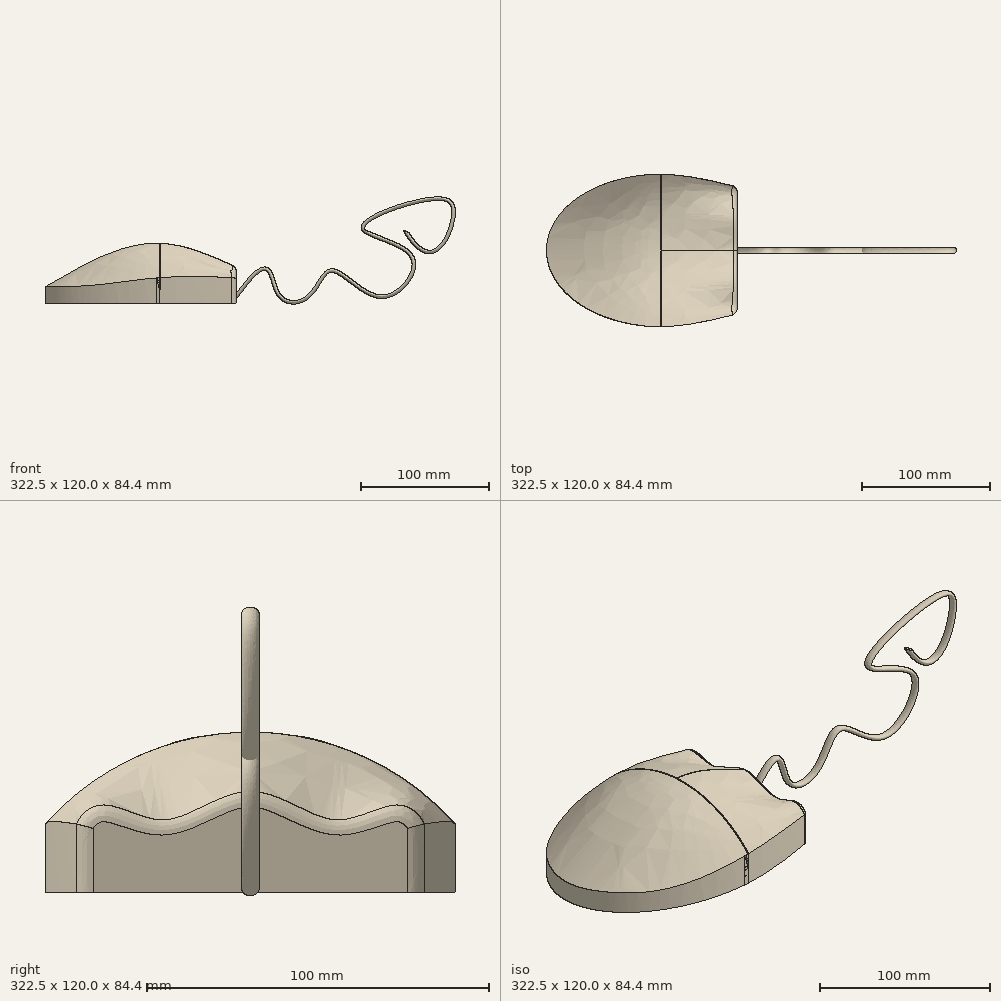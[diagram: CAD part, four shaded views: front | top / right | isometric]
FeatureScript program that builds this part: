
annotation { "Feature Type Name" : "Feature", "Feature Type Description" : "" }
export const myFeature = defineFeature(function(context is Context, id is Id, definition is map)
    precondition{}
    {
        {
            var Q0;
            Q0=qCreatedBy(makeId("Right.planeOp"),FACE);
            cPlane(context, id + "F0", {"entities" : qUnion([Q0]), "cplaneType" : CPlaneType.OFFSET, "offset" : 60 * mm, "width" : 150 * mm, "height" : 150 * mm});
        }
        {
            var Q0;
            Q0=qCreatedBy(makeId("Right.planeOp"),FACE);
            var Q1;
            Q1 = qBodyType(qCreatedBy(id + "F3" ,EDGE), BodyType.WIRE);
            cPlane(context, id + "F1", {"entities" : qUnion([Q0, Q1]), "cplaneType" : CPlaneType.OFFSET, "offset" : 90 * mm, "oppositeDirection" : true, "width" : 150 * mm, "height" : 150 * mm});
        }
        {
            var Q0;
            Q0=qCreatedBy(id+"F1.planeOp",FACE);
            var sketch = newSketch(context, id + "F2", { "sketchPlane" : qUnion([Q0])});
            skLineSegment(sketch, "E0", {"start": v(-40, 0) * mm, "end": v(-40, 2) * mm});
            skLineSegment(sketch, "E1", {"start": v(40, 2) * mm, "end": v(40, 0) * mm});
            skLineSegment(sketch, "E2", {"start": v(-40, 0) * mm, "end": v(40, 0) * mm});
            skArc(sketch, "E3", {"start": v(40, 2) * mm, "mid": v(0, 12.72) * mm, "end": v(-40, 2) * mm});
            skSolve(sketch);
        }
        {
            var Q0;
            Q0=qCreatedBy(id+"F0.planeOp",FACE);
            var sketch = newSketch(context, id + "F3", { "sketchPlane" : qUnion([Q0])});
            skLineSegment(sketch, "E4", {"start": v(-50, 0) * mm, "end": v(50, 0) * mm});
            skLineSegment(sketch, "E5", {"start": v(-50, 0) * mm, "end": v(-50, 20) * mm});
            skLineSegment(sketch, "E6", {"start": v(50, 20) * mm, "end": v(50, 0) * mm});
            skFitSpline(sketch, "E7", {"points": [v(-50, 20) * mm, v(-43, 25) * mm, v(-25, 20) * mm, v(0, 28.4) * mm, v(25, 20) * mm, v(43, 25) * mm, v(50, 20) * mm], "startDerivative": vector(27.74, 64.52) * mm, "endDerivative": vector(29, -66.62) * mm});
            skSolve(sketch);
        }
        {
            var Q0;
            Q0=qCreatedBy(makeId("Right.planeOp"),FACE);
            var sketch = newSketch(context, id + "F4", { "sketchPlane" : qUnion([Q0])});
            skLineSegment(sketch, "E8", {"start": v(-60, 0) * mm, "end": v(60, 0) * mm});
            skLineSegment(sketch, "E9", {"start": v(-60, 0) * mm, "end": v(-60, 20) * mm});
            skLineSegment(sketch, "E10", {"start": v(60, 20) * mm, "end": v(60, 0) * mm});
            skArc(sketch, "E11", {"start": v(60, 20) * mm, "mid": v(0, 47.08) * mm, "end": v(-60, 20) * mm});
            skSolve(sketch);
        }
        {
            var Q0;
            Q0=makeQuery(id+"F2.imprint","IMPRINT",FACE,{"disambiguationData":[TD([[makeQuery(id+"F2.imprint","IMPRINT",EDGE,{"derivedFrom":sQuery(id+"F2.wireOp",EDGE,"E0")}),-1.0]])]});
            var Q1;
            Q1=makeQuery(id+"F4.imprint","IMPRINT",FACE,{"disambiguationData":[TD([[makeQuery(id+"F4.imprint","IMPRINT",EDGE,{"derivedFrom":sQuery(id+"F4.wireOp",EDGE,"E8")}),1.0]])]});
            var Q2;
            Q2=makeQuery(id+"F3.imprint","IMPRINT",FACE,{"disambiguationData":[TD([[makeQuery(id+"F3.imprint","IMPRINT",EDGE,{"derivedFrom":sQuery(id+"F3.wireOp",EDGE,"E4")}),1.0]])]});
            loft(context, id + "F5", {"sheetProfilesArray" : [{ "sheetProfileEntities" : qUnion([Q0]) }, { "sheetProfileEntities" : qUnion([Q1]) }, { "sheetProfileEntities" : qUnion([Q2]) }]});
        }
        {
            var Q0;
            Q0=qCreatedBy(makeId("Top.planeOp"),FACE);
            cPlane(context, id + "F6", {"entities" : qUnion([Q0]), "cplaneType" : CPlaneType.OFFSET, "offset" : 47.08 * mm, "width" : 150 * mm, "height" : 150 * mm});
        }
        {
            var Q0;
            Q0=qCreatedBy(id+"F6.planeOp",FACE);
            var sketch = newSketch(context, id + "F7", { "sketchPlane" : qUnion([Q0])});
            skLineSegment(sketch, "E12.bottom", {"start": v(0, 60) * mm, "end": v(0.5, 60) * mm});
            skLineSegment(sketch, "E12.top", {"start": v(0, -60) * mm, "end": v(0.5, -60) * mm});
            skLineSegment(sketch, "E12.left", {"start": v(0, 60) * mm, "end": v(0, -60) * mm});
            skLineSegment(sketch, "E12.right", {"start": v(0.5, 60) * mm, "end": v(0.5, -60) * mm});
            skLineSegment(sketch, "E13.bottom", {"start": v(0, 0.25) * mm, "end": v(60, 0.25) * mm});
            skLineSegment(sketch, "E13.top", {"start": v(0, -0.25) * mm, "end": v(60, -0.25) * mm});
            skLineSegment(sketch, "E13.left", {"start": v(0, 0.25) * mm, "end": v(0, -0.25) * mm});
            skLineSegment(sketch, "E13.right", {"start": v(60, 0.25) * mm, "end": v(60, -0.25) * mm});
            skSolve(sketch);
        }
        {
            var Q0;
            Q0 = qSketchRegion(id + "F7", true);
            extrude(context, id + "F8", {"entities" : qUnion([Q0]), "operationType" : NewBodyOperationType.REMOVE, "oppositeDirection" : true, "depth" : 37 * mm, "offsetDistance" : 25 * mm});
        }
        {
            var Q0;
            Q0=qCreatedBy(makeId("Top.planeOp"),FACE);
            var sketch = newSketch(context, id + "F9", { "sketchPlane" : qUnion([Q0])});
            skEllipticalArc(sketch, "E14", {});
            skPoint(sketch, "E15", {"position": v(0, -60) * mm});
            skPoint(sketch, "E16", {"position": v(0, 60) * mm});
            skPoint(sketch, "E17", {"position": v(-89.99, -40.02) * mm});
            skPoint(sketch, "E18", {"position": v(-89.99, 39.96) * mm});
            skLineSegment(sketch, "E19", {"start": v(0, -60) * mm, "end": v(-96.03, -60) * mm});
            skLineSegment(sketch, "E20", {"start": v(0, 60) * mm, "end": v(-96.03, 60) * mm});
            skLineSegment(sketch, "E21", {"start": v(-96.03, 60) * mm, "end": v(-96.03, -60) * mm});
            const initialGuessF9  = {"E14": [0, 0, -1, 0, 0.09, 0.06, 4.71238898038469, 1.5707963267948966]};
            skSetInitialGuess(sketch, initialGuessF9);
            skSolve(sketch);
        }
        {
            var Q0;
            Q0 = qSketchRegion(id + "F9", true);
            extrude(context, id + "F10", {"entities" : qUnion([Q0]), "operationType" : NewBodyOperationType.REMOVE, "depth" : 25 * mm, "offsetDistance" : 25 * mm});
        }
        {
            var Q0;
            Q0=makeQuery(id+"F5.opLoft","MID_CAP_EDGE",EDGE,{"disambiguationData":[OSD([sQuery(id+"F3.wireOp",EDGE,"E4"),sQuery(id+"F3.wireOp",EDGE,"E5"),sQuery(id+"F3.wireOp",EDGE,"E7")])],"capPos":2.0});
            var Q1;
            Q1=makeQuery(id+"F5.opLoft","MID_CAP_EDGE",EDGE,{"disambiguationData":[OSD([sQuery(id+"F3.wireOp",EDGE,"E4"),sQuery(id+"F3.wireOp",EDGE,"E6"),sQuery(id+"F3.wireOp",EDGE,"E7")])],"capPos":2.0});
            var Q2;
            {var subQ4=sQuery(id+"F3.wireOp",EDGE,"E5");var subQ5=sQuery(id+"F3.wireOp",EDGE,"E6");var subQ6=sQuery(id+"F3.wireOp",EDGE,"E7");Q2=makeQuery(id+"F8.boolean.opBoolean","SPLIT",EDGE,{"disambiguationData":[TD([makeQuery(id+"F8.opExtrude","SWEPT_FACE",FACE,{"disambiguationData":[OSD([sQuery(id+"F7.wireOp",EDGE,"E13.bottom")])]})])],"derivedFrom":makeQuery(id+"F5.opLoft","MID_CAP_EDGE",EDGE,{"disambiguationData":[OSD([subQ4,subQ5,subQ6])],"capPos":2.0})});}
            var Q3;
            {var subQ4=sQuery(id+"F3.wireOp",EDGE,"E5");var subQ5=sQuery(id+"F3.wireOp",EDGE,"E6");var subQ6=sQuery(id+"F3.wireOp",EDGE,"E7");Q3=makeQuery(id+"F8.boolean.opBoolean","SPLIT",EDGE,{"disambiguationData":[TD([makeQuery(id+"F8.opExtrude","SWEPT_FACE",FACE,{"disambiguationData":[OSD([sQuery(id+"F7.wireOp",EDGE,"E13.top")])]})])],"derivedFrom":makeQuery(id+"F5.opLoft","MID_CAP_EDGE",EDGE,{"disambiguationData":[OSD([subQ4,subQ5,subQ6])],"capPos":2.0})});}
            fillet(context, id + "F11", {"entities" : qUnion([Q0, Q1, Q2, Q3]), "radius" : 5 * mm, "tangentPropagation" : true, "allowEdgeOverflow" : false});
        }
        {
            var Q0;
            Q0=makeQuery(id+"F5.opLoft","CAP_FACE",FACE,{"disambiguationData":[OSD([makeQuery(id+"F3.imprint","IMPRINT",FACE,{"disambiguationData":[TD([[makeQuery(id+"F3.imprint","IMPRINT",EDGE,{"derivedFrom":sQuery(id+"F3.wireOp",EDGE,"E4")}),1.0]])]})])],"isStart":true});
            var sketch = newSketch(context, id + "F12", { "sketchPlane" : qUnion([Q0])});
            skPoint(sketch, "E22", {"position": v(0, 10.08) * mm});
            skLineSegment(sketch, "E23", {"start": v(0, 10.08) * mm, "end": v(0, 0) * mm});
            skPoint(sketch, "E24", {"position": v(0, 5.04) * mm});
            skCircle(sketch, "E25", {"center": v(0, 5.04) * mm, "radius": 2.5 * mm});
            skSolve(sketch);
        }
        {
            var Q0;
            Q0=qCreatedBy(makeId("Front.planeOp"),FACE);
            var sketch = newSketch(context, id + "F13", { "sketchPlane" : qUnion([Q0])});
            skPoint(sketch, "E26", {"position": v(60, 5.04) * mm});
            skFitSpline(sketch, "E27", {"points": [v(60, 5.04) * mm, v(92.4, 8.7) * mm, v(116.74, 5.04) * mm, v(135.33, 25.33) * mm, v(175.47, 5.1) * mm, v(198.2, 36.16) * mm, v(160.31, 58.94) * mm, v(214.87, 81.9) * mm, v(230.75, 68.36) * mm, v(193.4, 56.5) * mm], "startDerivative": vector(810.92, 1122.65) * mm, "endDerivative": vector(-555.41, 916.67) * mm});
            skSolve(sketch);
        }
        {
            var Q0;
            {var subQ0=sQuery(id+"F12.wireOp",EDGE,"E25");var subQ1=sQuery(id+"F12.wireOp",EDGE,"E23");var subQ2=makeQuery(id+"F12.imprint","INTERSECT",VERTEX,{"disambiguationData":[OD(0.0)],"derivedFrom":[subQ1,subQ0]});Q0=makeQuery(id+"F12.imprint","IMPRINT",FACE,{"disambiguationData":[TD([[makeQuery(id+"F12.imprint","IMPRINT",EDGE,{"disambiguationData":[TD([[subQ2,-1.0]])],"derivedFrom":subQ1}),-1.0]])]});}
            var Q1;
            {var subQ0=sQuery(id+"F12.wireOp",EDGE,"E25");var subQ1=sQuery(id+"F12.wireOp",EDGE,"E23");var subQ2=makeQuery(id+"F12.imprint","INTERSECT",VERTEX,{"disambiguationData":[OD(0.0)],"derivedFrom":[subQ1,subQ0]});Q1=makeQuery(id+"F12.imprint","IMPRINT",FACE,{"disambiguationData":[TD([[makeQuery(id+"F12.imprint","IMPRINT",EDGE,{"disambiguationData":[TD([[subQ2,-1.0]])],"derivedFrom":subQ1}),1.0]])]});}
            var Q2;
            Q2=sQuery(id+"F13.wireOp",EDGE,"E27");
            sweep(context, id + "F14", {"operationType" : NewBodyOperationType.ADD, "profiles" : qUnion([Q0, Q1]), "path" : qUnion([Q2])});
        }
    });
